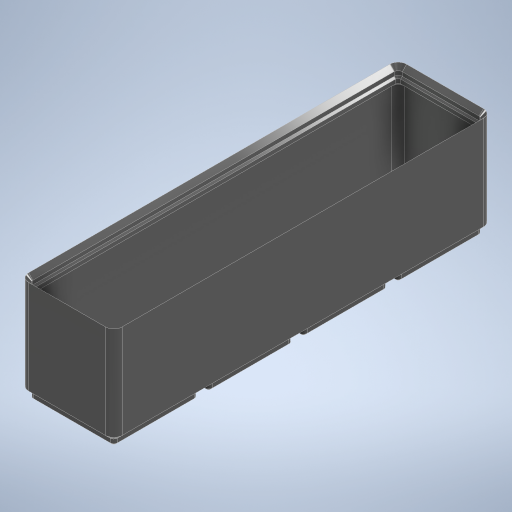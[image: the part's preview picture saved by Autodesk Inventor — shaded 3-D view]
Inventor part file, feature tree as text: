
AUTODESK INVENTOR PART (.ipt)
format: ipt  version: 2023 (Build 270158030, 158C)  size: 517,632 bytes
history: native  units: mm
features: extrude x14, sketch x14, projected_geometry x10, pattern_linear x1
ambient origin geometry x8: Origin, YZ Plane, XZ Plane, XY Plane, X Axis, Y Axis, Z Axis, Center Point
bodies: Solid2 (feature_tree)
feature tree (39):
  extrude  "base-generic"  Depth=41.5mm
  extrude  "Extrusion8"  Depth=3.75mm TaperAngle=0.0deg
  extrude  "Extrusion9"  Depth=2.15mm
  extrude  "Extrusion10"  Depth=0.8mm
  extrude  "Extrusion11"  Depth=7.75mm
  extrude  "Extrusion12"  Depth=7.75mm
  pattern_linear  "Rectangular Pattern1"  Count1=4 Spacing1=42.0mm
  extrude  "fill-gaps"  Depth=3.75mm
  extrude  "Extrusion14"  Depth=1.9mm
  extrude  "Extrusion15"  Depth=0.7mm
  extrude  "Extrusion16"  Depth=1.8mm TaperAngle=45.0deg
  extrude  "Extrusion17"  Depth=1.8mm TaperAngle=0.0deg
  extrude  "Extrusion18"  Depth=1.8mm
  extrude  "Extrusion19"  Depth=1.8mm
  extrude  "Extrusion20"  Depth=1.8mm
  sketch  "Sketch9"  dims[d50=41.5mm d51=41.5mm]
  sketch  "Sketch10"  dims[d52=3.75mm d53=2.25mm d54=0.0mm]
  projected_geometry  "Projected Loop2"
  sketch  "Sketch11"  dims[d55=3.75mm d56=2.15mm d57=-7.853982mm]
  projected_geometry  "Projected Loop3"
  sketch  "Sketch12"  dims[d58=1.8mm d59=0.0mm d60=0.8mm d61=-7.853982mm]
  projected_geometry  "Projected Loop4"
  sketch  "Sketch13"  dims[d62=6.5mm d63=7.75mm]
  sketch  "Sketch14"  dims[d64=7.75mm d65=7.75mm]
  sketch  "Sketch15"  dims[d66=7.75mm]
  sketch  "Sketch16"  dims[d67=2.4mm d68=0.0mm]
  projected_geometry  "Projected Loop5"
  sketch  "Sketch19"  dims[d69=3.0mm]
  projected_geometry  "Projected Loop8"
  sketch  "Sketch20"  dims[d70=6.0mm d71=0.0mm d72=40.0mm d74=42.0mm d75=10.0mm d77=42.0mm]
  projected_geometry  "Projected Loop9"
  sketch  "Sketch21"  dims[d79=2.25mm d80=0.0mm d82=3.75mm]
  projected_geometry  "Projected Loop10"
  sketch  "Sketch22"  dims[d83=39.4mm d84=0.0mm d87=1.9mm d88=-7.853982mm]
  projected_geometry  "Projected Loop11"
  sketch  "Sketch23"  dims[d89=1.8mm d90=0.0mm d91=0.7mm d92=-7.853982mm]
  projected_geometry  "Projected Loop12"
  sketch  "Sketch24"  dims[d93=1.8mm d94=0.0mm d95=1.8mm d96=45.0deg d97=33.0mm d98=0.0mm d17=0.5mm d18=0.872665mm d19=0.5mm d20=0.872665mm d24=0.0mm d25=0.0mm d26=0.0mm d27=0.0mm]
  projected_geometry  "Projected Loop13"
